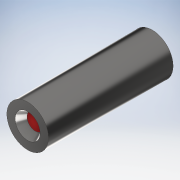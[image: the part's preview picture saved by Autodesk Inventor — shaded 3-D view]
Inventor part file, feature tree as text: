
AUTODESK INVENTOR PART (.ipt)
format: ipt  version: 2018 (Build 220112000, 112)  size: 124,416 bytes
history: native  units: mm
features: revolve x1, sketch x1
ambient origin geometry x8: Origin, YZ Plane, XZ Plane, XY Plane, X Axis, Y Axis, Z Axis, Center Point
bodies: Solid1 (feature_tree)
feature tree (2):
  revolve  "Revolution1"  [1 undecoded]
  sketch  "Sketch1"  dims[d0=7.0mm d1=21.0mm d2=90.0deg]
note: 1 required parameter value undecoded (feature->parameter linkage not recoverable at this tier; creation-order binding heuristic only, values carry confidence <= 0.55)
